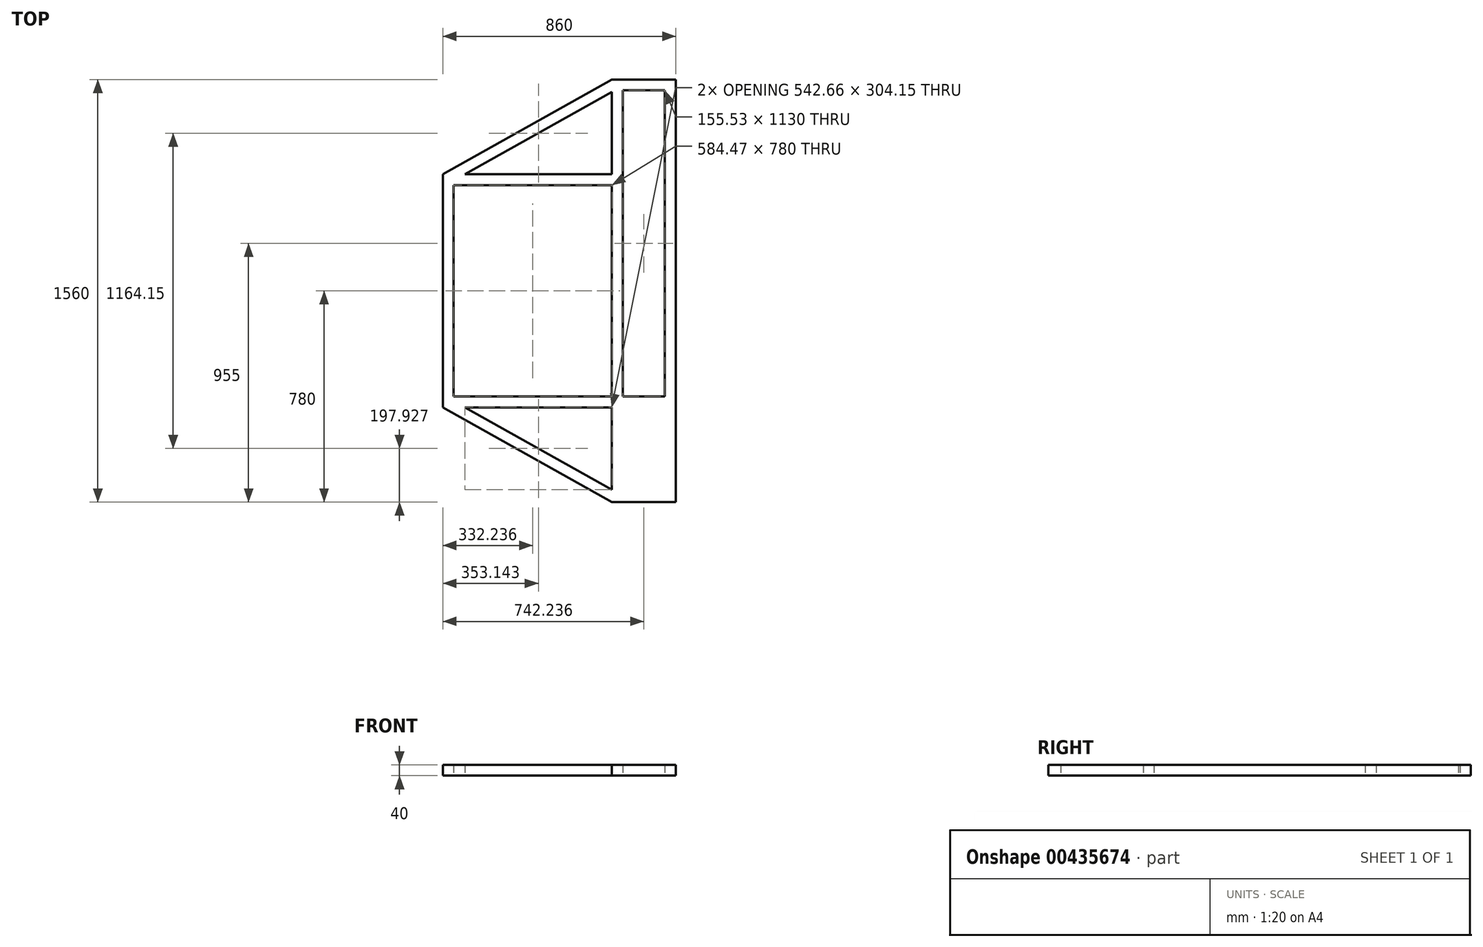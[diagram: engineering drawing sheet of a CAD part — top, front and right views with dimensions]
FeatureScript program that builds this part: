
annotation { "Feature Type Name" : "Feature", "Feature Type Description" : "" }
export const myFeature = defineFeature(function(context is Context, id is Id, definition is map)
    precondition{}
    {
        {
            var Q0;
            Q0=qCreatedBy(makeId("Top.planeOp"),FACE);
            var sketch = newSketch(context, id + "F0", { "sketchPlane" : qUnion([Q0])});
            skLineSegment(sketch, "E0.bottom", {"start": v(-390, 390) * mm, "end": v(390, 390) * mm});
            skLineSegment(sketch, "E0.top", {"start": v(-390, -390) * mm, "end": v(390, -390) * mm});
            skLineSegment(sketch, "E0.left", {"start": v(-390, 390) * mm, "end": v(-390, -390) * mm});
            skLineSegment(sketch, "E0.right", {"start": v(390, 390) * mm, "end": v(390, -390) * mm});
            skPoint(sketch, "E0.middle", {"position": v(0, 0) * mm});
            skLineSegment(sketch, "E1.0", {"start": v(-430, 430) * mm, "end": v(430, 430) * mm});
            skLineSegment(sketch, "E1.1", {"start": v(-430, 430) * mm, "end": v(-430, -430) * mm});
            skLineSegment(sketch, "E1.2", {"start": v(-430, -430) * mm, "end": v(430, -430) * mm});
            skLineSegment(sketch, "E1.3", {"start": v(430, 430) * mm, "end": v(430, -430) * mm});
            skLineSegment(sketch, "E2", {"start": v(430, 430) * mm, "end": v(194.47, 430) * mm});
            skLineSegment(sketch, "E3", {"start": v(430, 430) * mm, "end": v(430, 780) * mm});
            skLineSegment(sketch, "E4", {"start": v(430, 780) * mm, "end": v(194.47, 780) * mm});
            skLineSegment(sketch, "E5", {"start": v(194.47, 780) * mm, "end": v(-430, 430) * mm});
            skLineSegment(sketch, "E6", {"start": v(194.47, 780) * mm, "end": v(194.47, -430) * mm});
            skPoint(sketch, "E6.endSnap0", {"position": v(0, -430) * mm});
            skLineSegment(sketch, "E7", {"start": v(194.47, -430) * mm, "end": v(194.47, -780) * mm});
            skLineSegment(sketch, "E8", {"start": v(194.47, -780) * mm, "end": v(430, -780) * mm});
            skLineSegment(sketch, "E9", {"start": v(430, -780) * mm, "end": v(430, -430) * mm});
            skLineSegment(sketch, "E10", {"start": v(-430, -430) * mm, "end": v(194.47, -780) * mm});
            skLineSegment(sketch, "E11.0", {"start": v(193.17, 785) * mm, "end": v(-432.44, 434.36) * mm});
            skLineSegment(sketch, "E11.1", {"start": v(540, 785) * mm, "end": v(193.17, 785) * mm});
            skLineSegment(sketch, "E12.0", {"start": v(204.92, 740) * mm, "end": v(-410.44, 395.1) * mm});
            skLineSegment(sketch, "E12.1", {"start": v(390, 740) * mm, "end": v(204.92, 740) * mm});
            skLineSegment(sketch, "E12.2", {"start": v(390, 300) * mm, "end": v(390, 740) * mm});
            skLineSegment(sketch, "E13.0", {"start": v(390, -740) * mm, "end": v(390, -430) * mm});
            skLineSegment(sketch, "E13.1", {"start": v(204.92, -740) * mm, "end": v(390, -740) * mm});
            skLineSegment(sketch, "E13.2", {"start": v(-410.44, -395.1) * mm, "end": v(204.92, -740) * mm});
            skLineSegment(sketch, "E14.0", {"start": v(234.47, -300) * mm, "end": v(234.47, -650) * mm});
            skLineSegment(sketch, "E14.1", {"start": v(234.47, 780) * mm, "end": v(234.47, -300) * mm});
            skSolve(sketch);
        }
        {
            var Q0;
            Q0 = qSketchRegion(id + "F0", true);
            var Q1;
            {var subQ0=sQuery(id+"F0.wireOp",EDGE,"E6");var subQ1=sQuery(id+"F0.wireOp",EDGE,"E0.bottom");var subQ2=makeQuery(id+"F0.imprint","INTERSECT",VERTEX,{"derivedFrom":[subQ1,subQ0]});Q1=makeQuery(id+"F0.imprint","IMPRINT",FACE,{"disambiguationData":[TD([[makeQuery(id+"F0.imprint","IMPRINT",EDGE,{"disambiguationData":[TD([[subQ2,-1.0]])],"derivedFrom":subQ1}),-1.0]])]});}
            var Q2;
            {var subQ0=sQuery(id+"F0.wireOp",EDGE,"E12.1");var subQ1=sQuery(id+"F0.wireOp",EDGE,"E12.0");var subQ2=makeQuery(id+"F0.imprint","INTERSECT",VERTEX,{"derivedFrom":[subQ1,subQ0]});Q2=makeQuery(id+"F0.imprint","IMPRINT",FACE,{"disambiguationData":[TD([[makeQuery(id+"F0.imprint","IMPRINT",EDGE,{"disambiguationData":[TD([[subQ2,-1.0]])],"derivedFrom":subQ1}),1.0]])]});}
            var Q3;
            {var subQ0=sQuery(id+"F0.wireOp",EDGE,"E13.2");var subQ1=sQuery(id+"F0.wireOp",EDGE,"E13.1");var subQ2=makeQuery(id+"F0.imprint","INTERSECT",VERTEX,{"derivedFrom":[subQ1,subQ0]});Q3=makeQuery(id+"F0.imprint","IMPRINT",FACE,{"disambiguationData":[TD([[makeQuery(id+"F0.imprint","IMPRINT",EDGE,{"disambiguationData":[TD([[subQ2,-1.0]])],"derivedFrom":subQ1}),1.0]])]});}
            var Q4;
            {var subQ0=sQuery(id+"F0.wireOp",EDGE,"E6");var subQ1=sQuery(id+"F0.wireOp",EDGE,"E0.top");var subQ2=makeQuery(id+"F0.imprint","INTERSECT",VERTEX,{"derivedFrom":[subQ1,subQ0]});Q4=makeQuery(id+"F0.imprint","IMPRINT",FACE,{"disambiguationData":[TD([[makeQuery(id+"F0.imprint","IMPRINT",EDGE,{"disambiguationData":[TD([[subQ2,-1.0]])],"derivedFrom":subQ1}),-1.0]])]});}
            var Q5;
            {var subQ0=sQuery(id+"F0.wireOp",EDGE,"E6");var subQ1=sQuery(id+"F0.wireOp",EDGE,"E0.bottom");var subQ2=makeQuery(id+"F0.imprint","INTERSECT",VERTEX,{"derivedFrom":[subQ1,subQ0]});Q5=makeQuery(id+"F0.imprint","IMPRINT",FACE,{"disambiguationData":[TD([[makeQuery(id+"F0.imprint","IMPRINT",EDGE,{"disambiguationData":[TD([[subQ2,-1.0]])],"derivedFrom":subQ1}),1.0]])]});}
            extrude(context, id + "F1", {"entities" : qUnion([Q0, Q1, Q2, Q3, Q4, Q5]), "endBound" : BoundingType.SYMMETRIC, "depth" : 40 * mm});
        }
    });
